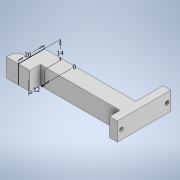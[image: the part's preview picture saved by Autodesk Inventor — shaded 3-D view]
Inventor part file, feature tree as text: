
AUTODESK INVENTOR PART (.ipt)
format: ipt  version: 2020.3 (Build 243373000, 373)  size: 268,288 bytes
history: native  units: mm
features: extrude x3, sketch x2, fillet x1
ambient origin geometry x8: Origin, YZ Plane, XZ Plane, XY Plane, X Axis, Y Axis, Z Axis, Center Point
bodies: Body1 (feature_tree)
feature tree (6):
  sketch  "Sketch1"  dims[d12=14.0mm d13=20.0mm]
  extrude  "Extrusion6"  Depth=20.0mm
  extrude  "Extrusion7"  TaperAngle=0.0deg  [1 undecoded]
  fillet  "Fillet1"  Radius=70.0mm
  extrude  "Extrusion8"  Depth=18.0mm TaperAngle=0.0deg
  sketch  "Sketch6"  dims[d14=12.0mm d15=0.0mm d16=70.0mm d17=0.0mm d18=18.0mm d19=0.0mm d20=5.0mm d21=41.0mm d22=2.8mm d23=3.0mm d24=2.8mm d25=35.0mm d26=5.0mm d27=6.0mm d28=0.0mm]
note: 1 required parameter value undecoded (feature->parameter linkage not recoverable at this tier; creation-order binding heuristic only, values carry confidence <= 0.55)
